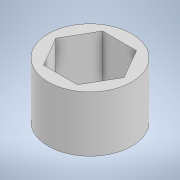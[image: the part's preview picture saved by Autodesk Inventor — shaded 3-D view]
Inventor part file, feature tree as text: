
AUTODESK INVENTOR PART (.ipt)
format: ipt  version: 2022.3 (Build 263350000, 350)  size: 100,864 bytes
history: native  units: in
note: dims shown in document units (in); Inventor stores cm internally (conversion verified against a paired STEP export)
features: extrude x1, sketch x1
ambient origin geometry x8: Origin, YZ Plane, XZ Plane, XY Plane, X Axis, Y Axis, Z Axis, Center Point
bodies: Solid1 (feature_tree)
feature tree (2):
  extrude  "Extrusion1"  Depth=0.5in
  sketch  "Sketch1"  dims[d0=0.53in d1=0.75in d2=0.5in d3=0.0in]
